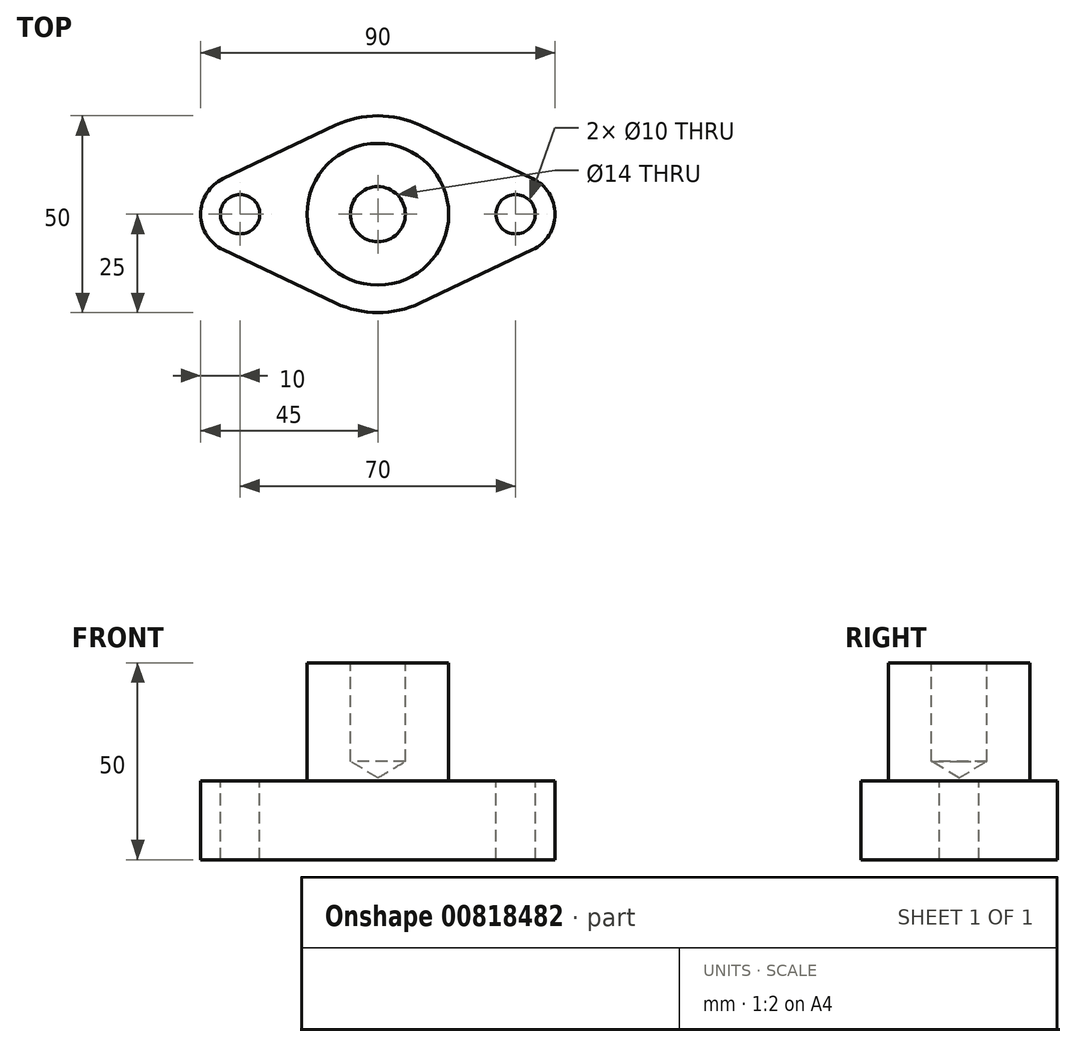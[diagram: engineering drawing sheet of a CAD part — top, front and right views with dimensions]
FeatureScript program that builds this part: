
annotation { "Feature Type Name" : "Feature", "Feature Type Description" : "" }
export const myFeature = defineFeature(function(context is Context, id is Id, definition is map)
    precondition{}
    {
        {
            var Q0;
            Q0=qCreatedBy(makeId("Top.planeOp"),FACE);
            var sketch = newSketch(context, id + "F0", { "sketchPlane" : qUnion([Q0])});
            skArc(sketch, "E0", {"start": v(-39.29, 9.04) * mm, "mid": v(-45, 0) * mm, "end": v(-39.29, -9.04) * mm});
            skArc(sketch, "E1", {"start": v(39.29, -9.04) * mm, "mid": v(45, 0) * mm, "end": v(39.29, 9.04) * mm});
            skArc(sketch, "E2", {"start": v(-10.71, -22.59) * mm, "mid": v(0, -25) * mm, "end": v(10.71, -22.59) * mm});
            skLineSegment(sketch, "E3", {"start": v(-39.29, 9.04) * mm, "end": v(-10.71, 22.59) * mm});
            skLineSegment(sketch, "E4", {"start": v(-39.29, -9.04) * mm, "end": v(-10.71, -22.59) * mm});
            skLineSegment(sketch, "E5", {"start": v(39.29, -9.04) * mm, "end": v(10.71, -22.59) * mm});
            skLineSegment(sketch, "E6", {"start": v(10.71, 22.59) * mm, "end": v(39.29, 9.04) * mm});
            skArc(sketch, "E7.trimOffspring", {"start": v(10.71, 22.59) * mm, "mid": v(0, 25) * mm, "end": v(-10.71, 22.59) * mm});
            skSolve(sketch);
        }
        {
            var Q0;
            {var subQ0=sQuery(id+"F0.wireOp",EDGE,"lmiAjQvb-wpT7-QrmH-ZmYd-Wv5TLuR0ynjM");var subQ1=sQuery(id+"F0.wireOp",EDGE,"joltSibT-4jND-OQzG-vvrP-nefYPTBqjP67");var subQ2=makeQuery(id+"F0.imprint","INTERSECT",VERTEX,{"derivedFrom":[subQ1,subQ0]});Q0=makeQuery(id+"F0.imprint","IMPRINT",FACE,{"disambiguationData":[TD([[makeQuery(id+"F0.imprint","IMPRINT",EDGE,{"disambiguationData":[TD([[subQ2,1.0]])],"derivedFrom":subQ1}),1.0]])]});}
            var Q1;
            Q1=makeQuery(id+"F0.imprint","IMPRINT",FACE,{"disambiguationData":[TD([[makeQuery(id+"F0.imprint","IMPRINT",EDGE,{"derivedFrom":sQuery(id+"F0.wireOp",EDGE,"dZIxbuhc-ilEF-9hom-m2KE-1IUj5S0s78BO")}),1.0]])]});
            var Q2;
            Q2=makeQuery(id+"F0.imprint","IMPRINT",FACE,{"disambiguationData":[TD([[makeQuery(id+"F0.imprint","IMPRINT",EDGE,{"derivedFrom":sQuery(id+"F0.wireOp",EDGE,"ZP69xi9b-izlr-SclE-TUdG-vdJtKJvvfQe9")}),1.0]])]});
            var Q3;
            {var subQ1=sQuery(id+"F0.wireOp",EDGE,"joltSibT-4jND-OQzG-vvrP-nefYPTBqjP67");var subQ7=sQuery(id+"F0.wireOp",EDGE,"lmiAjQvb-wpT7-QrmH-ZmYd-Wv5TLuR0ynjM");var subQ9=makeQuery(id+"F0.imprint","INTERSECT",VERTEX,{"derivedFrom":[subQ1,subQ7]});Q3=makeQuery(id+"F0.imprint","IMPRINT",FACE,{"disambiguationData":[TD([[makeQuery(id+"F0.imprint","IMPRINT",EDGE,{"disambiguationData":[TD([[subQ9,-1.0]])],"derivedFrom":subQ1}),-1.0]])]});}
            var Q4;
            Q4=makeQuery(id+"F0.imprint","IMPRINT",FACE,{"disambiguationData":[TD([[makeQuery(id+"F0.imprint","IMPRINT",EDGE,{"derivedFrom":sQuery(id+"F0.wireOp",EDGE,"dZIxbuhc-ilEF-9hom-m2KE-1IUj5S0s78BO")}),-1.0]])]});
            var Q5;
            {var subQ0=sQuery(id+"F0.wireOp",EDGE,"lmiAjQvb-wpT7-QrmH-ZmYd-Wv5TLuR0ynjM");var subQ1=sQuery(id+"F0.wireOp",EDGE,"joltSibT-4jND-OQzG-vvrP-nefYPTBqjP67");var subQ2=makeQuery(id+"F0.imprint","INTERSECT",VERTEX,{"derivedFrom":[subQ1,subQ0]});Q5=makeQuery(id+"F0.imprint","IMPRINT",FACE,{"disambiguationData":[TD([[makeQuery(id+"F0.imprint","IMPRINT",EDGE,{"disambiguationData":[TD([[subQ2,-1.0]])],"derivedFrom":subQ1}),1.0]])]});}
            var Q6;
            {var subQ0=sQuery(id+"F0.wireOp",EDGE,"E3");Q6=makeQuery(id+"F0.imprint","IMPRINT",FACE,{"disambiguationData":[TD([[makeQuery(id+"F0.imprint","IMPRINT",EDGE,{"derivedFrom":subQ0}),-1.0]])]});}
            var Q7;
            {var subQ0=sQuery(id+"F0.wireOp",EDGE,"E4");var subQ1=sQuery(id+"F0.wireOp",EDGE,"E0");var subQ2=makeQuery(id+"F0.imprint","INTERSECT",VERTEX,{"disambiguationData":[OD(1.0)],"derivedFrom":[subQ1,subQ0]});Q7=makeQuery(id+"F0.imprint","IMPRINT",FACE,{"disambiguationData":[TD([[makeQuery(id+"F0.imprint","IMPRINT",EDGE,{"disambiguationData":[TD([[subQ2,-1.0]])],"derivedFrom":subQ0}),1.0]])]});}
            var Q8;
            {var subQ0=sQuery(id+"F0.wireOp",EDGE,"E6");Q8=makeQuery(id+"F0.imprint","IMPRINT",FACE,{"disambiguationData":[TD([[makeQuery(id+"F0.imprint","IMPRINT",EDGE,{"derivedFrom":subQ0}),-1.0]])]});}
            var Q9;
            {var subQ0=sQuery(id+"F0.wireOp",EDGE,"E5");var subQ1=sQuery(id+"F0.wireOp",EDGE,"E1");var subQ2=makeQuery(id+"F0.imprint","INTERSECT",VERTEX,{"derivedFrom":[subQ1,subQ0]});Q9=makeQuery(id+"F0.imprint","IMPRINT",FACE,{"disambiguationData":[TD([[makeQuery(id+"F0.imprint","IMPRINT",EDGE,{"disambiguationData":[TD([[subQ2,-1.0]])],"derivedFrom":subQ0}),-1.0]])]});}
            var Q10;
            Q10=makeQuery(id+"F0.imprint","IMPRINT",FACE,{"disambiguationData":[TD([[makeQuery(id+"F0.imprint","IMPRINT",EDGE,{"derivedFrom":sQuery(id+"F0.wireOp",EDGE,"ZP69xi9b-izlr-SclE-TUdG-vdJtKJvvfQe9")}),-1.0]])]});
            var Q11;
            {var subQ0=sQuery(id+"F0.wireOp",EDGE,"E4");var subQ1=sQuery(id+"F0.wireOp",EDGE,"E0");var subQ2=makeQuery(id+"F0.imprint","INTERSECT",VERTEX,{"disambiguationData":[OD(0.0)],"derivedFrom":[subQ1,subQ0]});Q11=makeQuery(id+"F0.imprint","IMPRINT",FACE,{"disambiguationData":[TD([[makeQuery(id+"F0.imprint","IMPRINT",EDGE,{"disambiguationData":[TD([[subQ2,-1.0]])],"derivedFrom":subQ1}),1.0]])]});}
            var Q12;
            {var subQ0=sQuery(id+"F0.wireOp",EDGE,"E4");var subQ1=sQuery(id+"F0.wireOp",EDGE,"E2");var subQ2=makeQuery(id+"F0.imprint","INTERSECT",VERTEX,{"disambiguationData":[OD(0.0)],"derivedFrom":[subQ1,subQ0]});Q12=makeQuery(id+"F0.imprint","IMPRINT",FACE,{"disambiguationData":[TD([[makeQuery(id+"F0.imprint","IMPRINT",EDGE,{"disambiguationData":[TD([[subQ2,1.0]])],"derivedFrom":subQ1}),1.0]])]});}
            var Q13;
            {var subQ0=sQuery(id+"F0.wireOp",EDGE,"E5");var subQ1=sQuery(id+"F0.wireOp",EDGE,"E2");var subQ2=makeQuery(id+"F0.imprint","INTERSECT",VERTEX,{"disambiguationData":[OD(0.0)],"derivedFrom":[subQ1,subQ0]});Q13=makeQuery(id+"F0.imprint","IMPRINT",FACE,{"disambiguationData":[TD([[makeQuery(id+"F0.imprint","IMPRINT",EDGE,{"disambiguationData":[TD([[subQ2,-1.0]])],"derivedFrom":subQ1}),1.0]])]});}
            var Q14;
            {var subQ0=sQuery(id+"F0.wireOp",EDGE,"lmiAjQvb-wpT7-QrmH-ZmYd-Wv5TLuR0ynjM");var subQ1=sQuery(id+"F0.wireOp",EDGE,"joltSibT-4jND-OQzG-vvrP-nefYPTBqjP67");var subQ2=makeQuery(id+"F0.imprint","INTERSECT",VERTEX,{"derivedFrom":[subQ1,subQ0]});Q14=makeQuery(id+"F0.imprint","IMPRINT",FACE,{"disambiguationData":[TD([[makeQuery(id+"F0.imprint","IMPRINT",EDGE,{"disambiguationData":[TD([[subQ2,1.0]])],"derivedFrom":subQ1}),-1.0]])]});}
            extrude(context, id + "F1", {"entities" : qUnion([Q0, Q1, Q2, Q3, Q4, Q5, Q6, Q7, Q8, Q9, Q10, Q11, Q12, Q13, Q14]), "oppositeDirection" : true, "depth" : 20 * mm, "offsetDistance" : 25 * mm});
        }
        {
            var Q0;
            Q0=makeQuery(id+"F1.opExtrude","SWEPT_BODY",BODY,{"disambiguationData":[OSD([sQuery(id+"F0.wireOp",EDGE,"E0"),sQuery(id+"F0.wireOp",EDGE,"E1"),sQuery(id+"F0.wireOp",EDGE,"E2"),sQuery(id+"F0.wireOp",EDGE,"E3"),sQuery(id+"F0.wireOp",EDGE,"E4"),sQuery(id+"F0.wireOp",EDGE,"E5"),sQuery(id+"F0.wireOp",EDGE,"E6")])]});
            var Q1;
            Q1=makeQuery(id+"F1.opExtrude","SWEPT_EDGE",EDGE,{"disambiguationData":[OSD([sQuery(id+"F0.wireOp",EDGE,"E0"),sQuery(id+"F0.wireOp",EDGE,"E3")])]});
            transform(context, id + "F2", {"entities" : qUnion([Q0]), "transformType" : TransformType.TRANSLATION_DISTANCE, "transformDirection" : qUnion([Q1]), "distance" : 20 * mm, "makeCopy" : false});
        }
        {
            var Q0;
            Q0=makeQuery(id+"F1.opExtrude","CAP_FACE",FACE,{"disambiguationData":[OSD([sQuery(id+"F0.wireOp",EDGE,"E0"),sQuery(id+"F0.wireOp",EDGE,"E1"),sQuery(id+"F0.wireOp",EDGE,"E2"),sQuery(id+"F0.wireOp",EDGE,"E3"),sQuery(id+"F0.wireOp",EDGE,"E4"),sQuery(id+"F0.wireOp",EDGE,"E5"),sQuery(id+"F0.wireOp",EDGE,"E6"),sQuery(id+"F0.wireOp",EDGE,"E7.trimOffspring")])],"isStart":true});
            var sketch = newSketch(context, id + "F3", { "sketchPlane" : qUnion([Q0])});
            skCircle(sketch, "E8", {"center": v(0, 0) * mm, "radius": 18 * mm});
            skPoint(sketch, "E9", {"position": v(35, 0) * mm});
            skPoint(sketch, "E10", {"position": v(-35, 0) * mm});
            skSolve(sketch);
        }
        {
            var Q0;
            Q0=makeQuery(id+"F3.imprint","IMPRINT",FACE,{"disambiguationData":[TD([[makeQuery(id+"F3.imprint","IMPRINT",EDGE,{"derivedFrom":sQuery(id+"F3.wireOp",EDGE,"E8")}),1.0]])]});
            extrude(context, id + "F4", {"entities" : qUnion([Q0]), "operationType" : NewBodyOperationType.ADD, "depth" : 30 * mm, "offsetDistance" : 25 * mm});
        }
        {
            var Q0;
            Q0=makeQuery(id+"F4.opExtrude","CAP_FACE",FACE,{"disambiguationData":[OSD([sQuery(id+"F3.wireOp",EDGE,"E8")])],"isStart":false});
            var sketch = newSketch(context, id + "F5", { "sketchPlane" : qUnion([Q0])});
            skPoint(sketch, "E11", {"position": v(0, 0) * mm});
            skSolve(sketch);
        }
        {
            var Q0;
            Q0=sQuery(id+"F5.wireOp",VERTEX,"E11");
            var Q1;
            Q1=makeQuery(id+"F1.opExtrude","SWEPT_BODY",BODY,{"disambiguationData":[OSD([sQuery(id+"F0.wireOp",EDGE,"E0"),sQuery(id+"F0.wireOp",EDGE,"E1"),sQuery(id+"F0.wireOp",EDGE,"E2"),sQuery(id+"F0.wireOp",EDGE,"E3"),sQuery(id+"F0.wireOp",EDGE,"E4"),sQuery(id+"F0.wireOp",EDGE,"E5"),sQuery(id+"F0.wireOp",EDGE,"E6"),sQuery(id+"F0.wireOp",EDGE,"E7.trimOffspring")])]});
            hole(context, id + "F6", {"style" : HoleStyle.SIMPLE, "endStyle" : HoleEndStyle.BLIND, "standardTappedOrClearance" : lookupTablePath({ "standard" : "ISO", "engagement" : "75%", "pitch" : "2 mm", "size" : "M16", "type" : "Tapped" }), "standardBlindInLast" : lookupTablePath({ "standard" : "ISO", "engagement" : "75%", "pitch" : "2 mm", "size" : "M16", "type" : "Tapped" }), "holeDiameter" : 14 * mm, "majorDiameter" : 16 * mm, "showTappedDepth" : true, "holeDepth" : 25 * mm, "isTappedThrough" : true, "tappedDepth" : 19 * mm, "tapClearance" : 3, "locations" : qUnion([Q0]), "scope" : qUnion([Q1])});
        }
        {
            var Q0;
            Q0=sQuery(id+"F3.wireOp",VERTEX,"E10");
            var Q1;
            Q1=sQuery(id+"F3.wireOp",VERTEX,"E9");
            var Q2;
            Q2=makeQuery(id+"F1.opExtrude","SWEPT_BODY",BODY,{"disambiguationData":[OSD([sQuery(id+"F0.wireOp",EDGE,"E0"),sQuery(id+"F0.wireOp",EDGE,"E1"),sQuery(id+"F0.wireOp",EDGE,"E2"),sQuery(id+"F0.wireOp",EDGE,"E3"),sQuery(id+"F0.wireOp",EDGE,"E4"),sQuery(id+"F0.wireOp",EDGE,"E5"),sQuery(id+"F0.wireOp",EDGE,"E6"),sQuery(id+"F0.wireOp",EDGE,"E7.trimOffspring")])]});
            hole(context, id + "F7", {"style" : HoleStyle.SIMPLE, "endStyle" : HoleEndStyle.THROUGH, "holeDiameter" : 10 * mm, "majorDiameter" : 16 * mm, "isTappedThrough" : true, "tappedDepth" : 19 * mm, "tapClearance" : 3, "locations" : qUnion([Q0, Q1]), "scope" : qUnion([Q2])});
        }
    });
